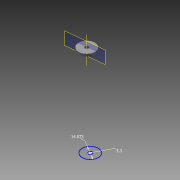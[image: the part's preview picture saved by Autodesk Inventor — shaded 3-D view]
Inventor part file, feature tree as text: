
AUTODESK INVENTOR PART (.ipt)
format: ipt  version: 2012 (Build 160160000, 160)  size: 79,360 bytes
history: native  units: mm
features: extrude x1, sketch x1
ambient origin geometry x8: Origin, YZ Plane, XZ Plane, XY Plane, X Axis, Y Axis, Z Axis, Center Point
bodies: Solid1 (feature_tree)
feature tree (2):
  extrude  "Extrusion7"  Depth=3.3mm
  sketch  "Sketch11"  dims[d14=14.073mm d15=3.3mm d16=2.0mm d17=0.0mm]
